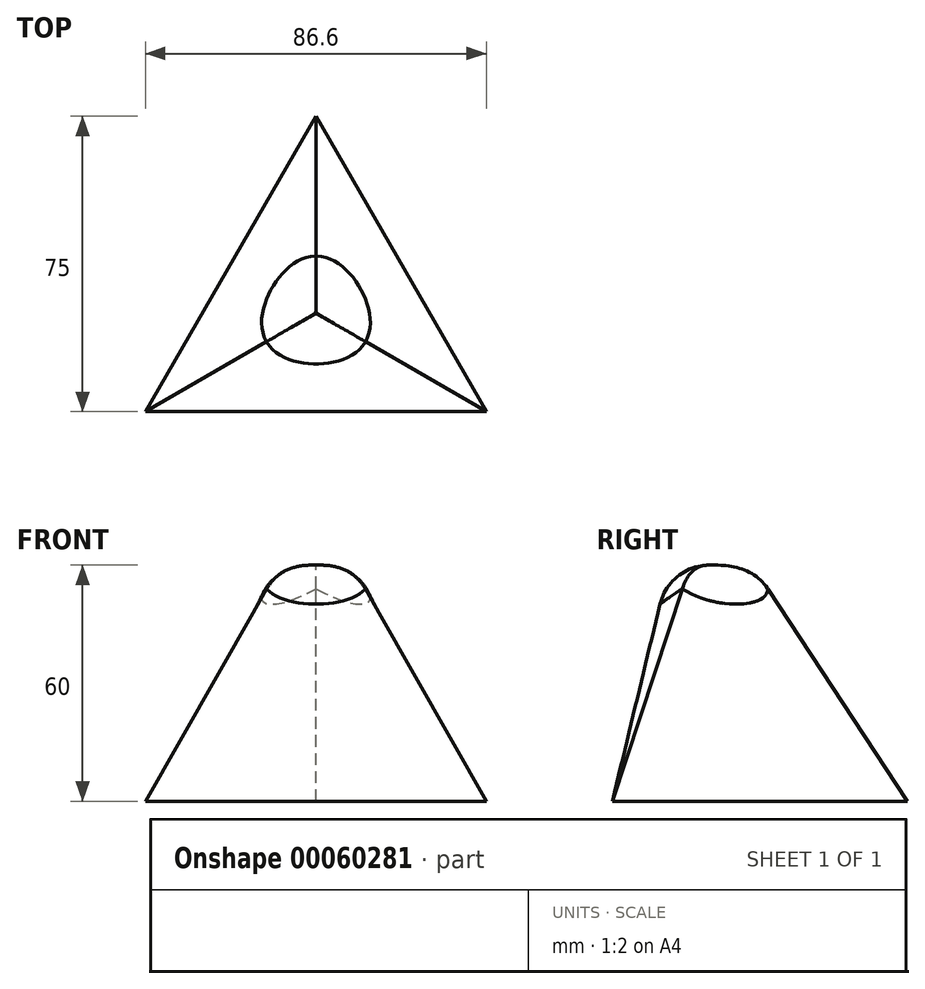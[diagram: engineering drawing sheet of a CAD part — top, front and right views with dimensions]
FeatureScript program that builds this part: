
annotation { "Feature Type Name" : "Feature", "Feature Type Description" : "" }
export const myFeature = defineFeature(function(context is Context, id is Id, definition is map)
    precondition{}
    {
        {
            var Q0;
            Q0=qCreatedBy(makeId("Top.planeOp"),FACE);
            cPlane(context, id + "F0", {"entities" : qUnion([Q0]), "cplaneType" : CPlaneType.OFFSET, "offset" : 60 * mm, "width" : 150 * mm, "height" : 150 * mm});
        }
        {
            var Q0;
            Q0=qCreatedBy(makeId("Top.planeOp"),FACE);
            var sketch = newSketch(context, id + "F1", { "sketchPlane" : qUnion([Q0])});
            skLineSegment(sketch, "E0.0", {"start": v(0, 50) * mm, "end": v(43.3, -25) * mm});
            skLineSegment(sketch, "E0.1", {"start": v(43.3, -25) * mm, "end": v(-43.3, -25) * mm});
            skLineSegment(sketch, "E0.2", {"start": v(-43.3, -25) * mm, "end": v(0, 50) * mm});
            skSolve(sketch);
        }
        {
            var Q0;
            Q0=qCreatedBy(id+"F0.planeOp",FACE);
            var sketch = newSketch(context, id + "F2", { "sketchPlane" : qUnion([Q0])});
            skCircle(sketch, "E1", {"center": v(0, 0) * mm, "radius": 10.48 * mm});
            skSolve(sketch);
        }
        {
            var Q0;
            Q0=makeQuery(id+"F1.imprint","IMPRINT",FACE,{"disambiguationData":[TD([[makeQuery(id+"F1.imprint","IMPRINT",EDGE,{"derivedFrom":sQuery(id+"F1.wireOp",EDGE,"E0.0")}),-1.0]])]});
            var Q1;
            Q1=makeQuery(id+"F2.imprint","IMPRINT",FACE,{"disambiguationData":[TD([[makeQuery(id+"F2.imprint","IMPRINT",EDGE,{"derivedFrom":sQuery(id+"F2.wireOp",EDGE,"E1")}),1.0]])]});
            loft(context, id + "F3", {"sheetProfilesArray" : [{ "sheetProfileEntities" : qUnion([Q0]) }, { "sheetProfileEntities" : qUnion([Q1]) }]});
        }
        {
            var Q0;
            Q0=makeQuery(id+"F3.opLoft","CAP_FACE",FACE,{"disambiguationData":[OSD([makeQuery(id+"F2.imprint","IMPRINT",FACE,{"disambiguationData":[TD([[makeQuery(id+"F2.imprint","IMPRINT",EDGE,{"derivedFrom":sQuery(id+"F2.wireOp",EDGE,"E1")}),1.0]])]})])],"isStart":true});
            fillet(context, id + "F4", {"entities" : qUnion([Q0]), "radius" : 13 * mm, "tangentPropagation" : true, "allowEdgeOverflow" : false});
        }
    });
